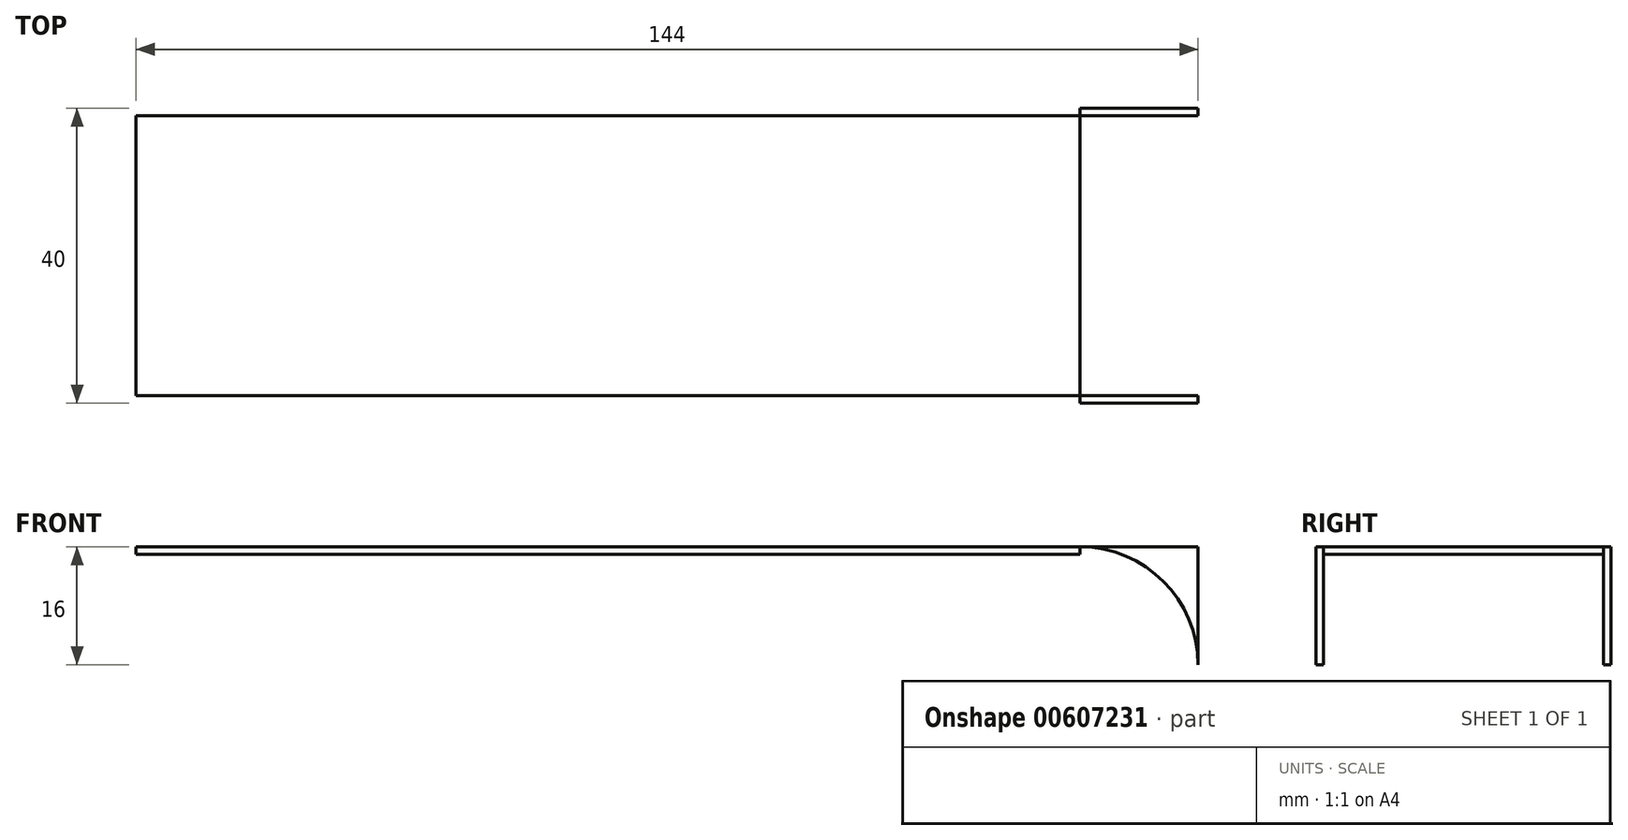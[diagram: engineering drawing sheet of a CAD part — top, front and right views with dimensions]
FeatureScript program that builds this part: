
annotation { "Feature Type Name" : "Feature", "Feature Type Description" : "" }
export const myFeature = defineFeature(function(context is Context, id is Id, definition is map)
    precondition{}
    {
        {
            var Q0;
            Q0=qCreatedBy(makeId("Top.planeOp"),FACE);
            var sketch = newSketch(context, id + "F0", { "sketchPlane" : qUnion([Q0])});
            skLineSegment(sketch, "E0.bottom", {"start": v(80, 19) * mm, "end": v(-80, 19) * mm});
            skLineSegment(sketch, "E0.top", {"start": v(80, -19) * mm, "end": v(-80, -19) * mm});
            skLineSegment(sketch, "E0.left", {"start": v(80, 19) * mm, "end": v(80, -19) * mm});
            skLineSegment(sketch, "E0.right", {"start": v(-80, 19) * mm, "end": v(-80, -19) * mm});
            skPoint(sketch, "E0.middle", {"position": v(0, 0) * mm});
            skSolve(sketch);
        }
        {
            var Q0;
            Q0 = qSketchRegion(id + "F0", true);
            extrude(context, id + "F1", {"entities" : qUnion([Q0]), "depth" : 1 * mm, "offsetDistance" : 25 * mm});
        }
        {
            var Q0;
            Q0=makeQuery(id+"F1.opExtrude","SWEPT_FACE",FACE,{"disambiguationData":[OSD([sQuery(id+"F0.wireOp",EDGE,"E0.top")])]});
            var sketch = newSketch(context, id + "F2", { "sketchPlane" : qUnion([Q0])});
            skLineSegment(sketch, "E1.bottom", {"start": v(-80, 32) * mm, "end": v(80, 32) * mm});
            skLineSegment(sketch, "E1.top", {"start": v(-80, 0) * mm, "end": v(80, 0) * mm});
            skLineSegment(sketch, "E1.left", {"start": v(-80, 32) * mm, "end": v(-80, 0) * mm});
            skLineSegment(sketch, "E1.right", {"start": v(80, 32) * mm, "end": v(80, 0) * mm});
            skSolve(sketch);
        }
        {
            var Q0;
            Q0 = qSketchRegion(id + "F2", true);
            extrude(context, id + "F3", {"entities" : qUnion([Q0]), "operationType" : NewBodyOperationType.ADD, "depth" : 1 * mm, "offsetDistance" : 25 * mm});
        }
        {
            var Q0;
            Q0=makeQuery(id+"F1.opExtrude","SWEPT_FACE",FACE,{"disambiguationData":[OSD([sQuery(id+"F0.wireOp",EDGE,"E0.bottom")])]});
            var sketch = newSketch(context, id + "F4", { "sketchPlane" : qUnion([Q0])});
            skLineSegment(sketch, "E2.bottom", {"start": v(80, 32) * mm, "end": v(-80, 32) * mm});
            skLineSegment(sketch, "E2.top", {"start": v(80, 0) * mm, "end": v(-80, 0) * mm});
            skLineSegment(sketch, "E2.left", {"start": v(80, 32) * mm, "end": v(80, 0) * mm});
            skLineSegment(sketch, "E2.right", {"start": v(-80, 32) * mm, "end": v(-80, 0) * mm});
            skSolve(sketch);
        }
        {
            var Q0;
            Q0 = qSketchRegion(id + "F4", true);
            extrude(context, id + "F5", {"entities" : qUnion([Q0]), "operationType" : NewBodyOperationType.ADD, "depth" : 1 * mm, "offsetDistance" : 25 * mm});
        }
        {
            var Q0;
            Q0=makeQuery(id+"F3.opExtrude","CAP_FACE",FACE,{"disambiguationData":[OSD([sQuery(id+"F2.wireOp",EDGE,"E1.bottom"),sQuery(id+"F2.wireOp",EDGE,"E1.top"),sQuery(id+"F2.wireOp",EDGE,"E1.left"),sQuery(id+"F2.wireOp",EDGE,"E1.right")])],"isStart":false});
            var sketch = newSketch(context, id + "F6", { "sketchPlane" : qUnion([Q0])});
            skArc(sketch, "E3", {"start": v(-64, 32) * mm, "mid": v(-75.31, 27.31) * mm, "end": v(-80, 16) * mm});
            skArc(sketch, "E4", {"start": v(64, 32) * mm, "mid": v(75.31, 27.31) * mm, "end": v(80, 16) * mm});
            skSolve(sketch);
        }
        {
            var Q0;
            {var subQ0=sQuery(id+"F6.wireOp",EDGE,"E3");Q0=makeQuery(id+"F6.imprint","IMPRINT",FACE,{"disambiguationData":[TD([[makeQuery(id+"F6.imprint","IMPRINT",EDGE,{"derivedFrom":subQ0}),-1.0]])]});}
            extrude(context, id + "F7", {"entities" : qUnion([Q0]), "operationType" : NewBodyOperationType.REMOVE, "endBound" : BoundingType.THROUGH_ALL, "oppositeDirection" : true, "depth" : 25 * mm, "offsetDistance" : 25 * mm});
        }
        {
            var Q0;
            {var subQ0=sQuery(id+"F6.wireOp",EDGE,"E4");Q0=makeQuery(id+"F6.imprint","IMPRINT",FACE,{"disambiguationData":[TD([[makeQuery(id+"F6.imprint","IMPRINT",EDGE,{"derivedFrom":subQ0}),1.0]])]});}
            extrude(context, id + "F8", {"entities" : qUnion([Q0]), "operationType" : NewBodyOperationType.REMOVE, "endBound" : BoundingType.THROUGH_ALL, "oppositeDirection" : true, "depth" : 1 * mm, "offsetDistance" : 25 * mm});
        }
        {
            var Q0;
            Q0=makeQuery(id+"F3.opExtrude","CAP_FACE",FACE,{"disambiguationData":[OSD([sQuery(id+"F2.wireOp",EDGE,"E1.bottom"),sQuery(id+"F2.wireOp",EDGE,"E1.top"),sQuery(id+"F2.wireOp",EDGE,"E1.left"),sQuery(id+"F2.wireOp",EDGE,"E1.right")])],"isStart":true});
            var sketch = newSketch(context, id + "F9", { "sketchPlane" : qUnion([Q0])});
            skLineSegment(sketch, "E5.bottom", {"start": v(-64, 32) * mm, "end": v(64, 32) * mm});
            skLineSegment(sketch, "E5.top", {"start": v(-64, 31) * mm, "end": v(64, 31) * mm});
            skLineSegment(sketch, "E5.left", {"start": v(-64, 32) * mm, "end": v(-64, 31) * mm});
            skLineSegment(sketch, "E5.right", {"start": v(64, 32) * mm, "end": v(64, 31) * mm});
            skSolve(sketch);
        }
        {
            var Q0;
            Q0 = qSketchRegion(id + "F9", true);
            extrude(context, id + "F10", {"entities" : qUnion([Q0]), "operationType" : NewBodyOperationType.ADD, "depth" : 38 * mm, "offsetDistance" : 25 * mm});
        }
    });
